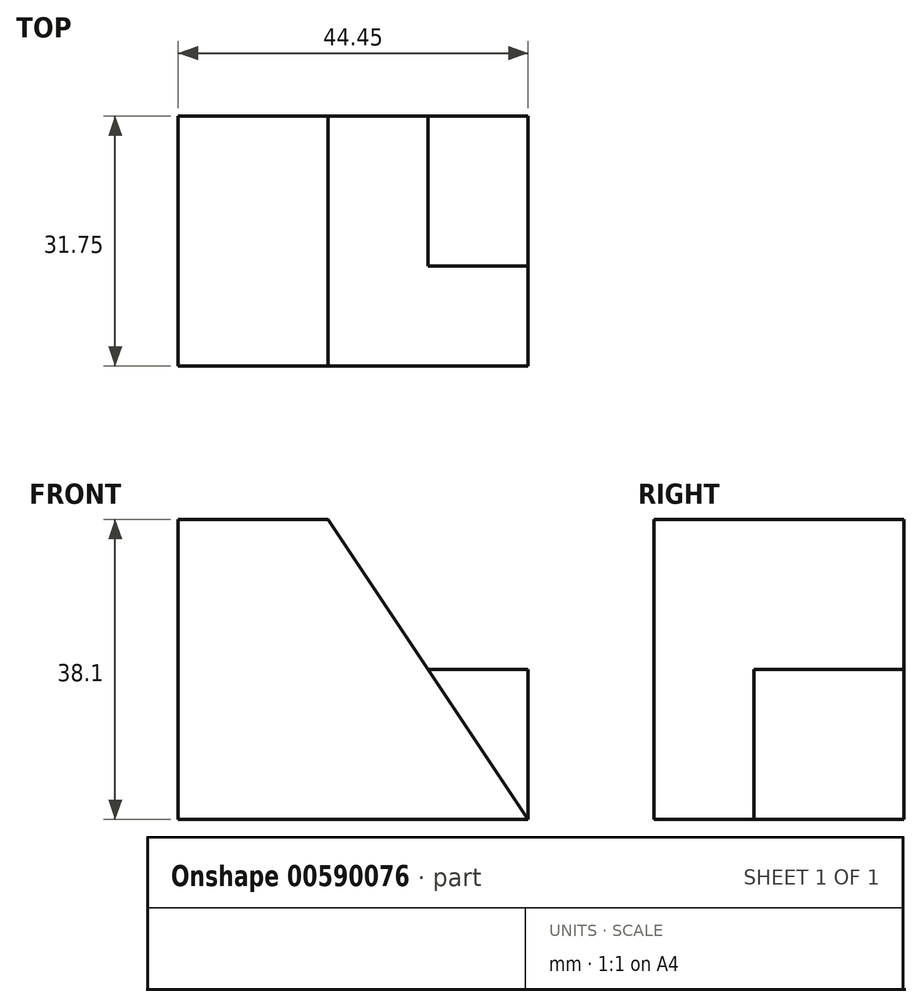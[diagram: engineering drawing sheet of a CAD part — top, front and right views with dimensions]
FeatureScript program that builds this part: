
annotation { "Feature Type Name" : "Feature", "Feature Type Description" : "" }
export const myFeature = defineFeature(function(context is Context, id is Id, definition is map)
    precondition{}
    {
        {
            var Q0;
            Q0=qCreatedBy(makeId("Front.planeOp"),FACE);
            var sketch = newSketch(context, id + "F0", { "sketchPlane" : qUnion([Q0])});
            skLineSegment(sketch, "E0", {"start": v(-58.81, 58.46) * mm, "end": v(-58.81, 20.36) * mm});
            skLineSegment(sketch, "E1", {"start": v(-58.81, 20.36) * mm, "end": v(-14.36, 20.36) * mm});
            skLineSegment(sketch, "E2", {"start": v(-14.36, 20.36) * mm, "end": v(-39.76, 58.46) * mm});
            skLineSegment(sketch, "E3", {"start": v(-39.76, 58.46) * mm, "end": v(-58.81, 58.46) * mm});
            skSolve(sketch);
        }
        {
            var Q0;
            Q0=makeQuery(id+"F0.imprint","IMPRINT",FACE,{"disambiguationData":[TD([[makeQuery(id+"F0.imprint","IMPRINT",EDGE,{"derivedFrom":sQuery(id+"F0.wireOp",EDGE,"E0")}),1.0]])]});
            extrude(context, id + "F1", {"entities" : qUnion([Q0]), "depth" : 31.75 * mm, "offsetDistance" : 25.4 * mm});
        }
        {
            var Q0;
            Q0=makeQuery(id+"F1.opExtrude","SWEPT_FACE",FACE,{"disambiguationData":[OSD([sQuery(id+"F0.wireOp",EDGE,"E0")])]});
            var sketch = newSketch(context, id + "F2", { "sketchPlane" : qUnion([Q0])});
            skLineSegment(sketch, "E4", {"start": v(19.05, 20.36) * mm, "end": v(19.05, 39.41) * mm});
            skLineSegment(sketch, "E5", {"start": v(19.05, 39.41) * mm, "end": v(0, 39.41) * mm});
            skSolve(sketch);
        }
        {
            var Q0;
            Q0 = qSketchRegion(id + "F2", true);
            var Q1;
            {var subQ0=sQuery(id+"F2.wireOp",EDGE,"E4");Q1=makeQuery(id+"F2.imprint","IMPRINT",FACE,{"disambiguationData":[TD([[makeQuery(id+"F2.imprint","IMPRINT",EDGE,{"derivedFrom":subQ0}),1.0]])]});}
            extrude(context, id + "F3", {"entities" : qUnion([Q0, Q1]), "operationType" : NewBodyOperationType.ADD, "oppositeDirection" : true, "depth" : 44.45 * mm, "offsetDistance" : 25.4 * mm});
        }
    });
